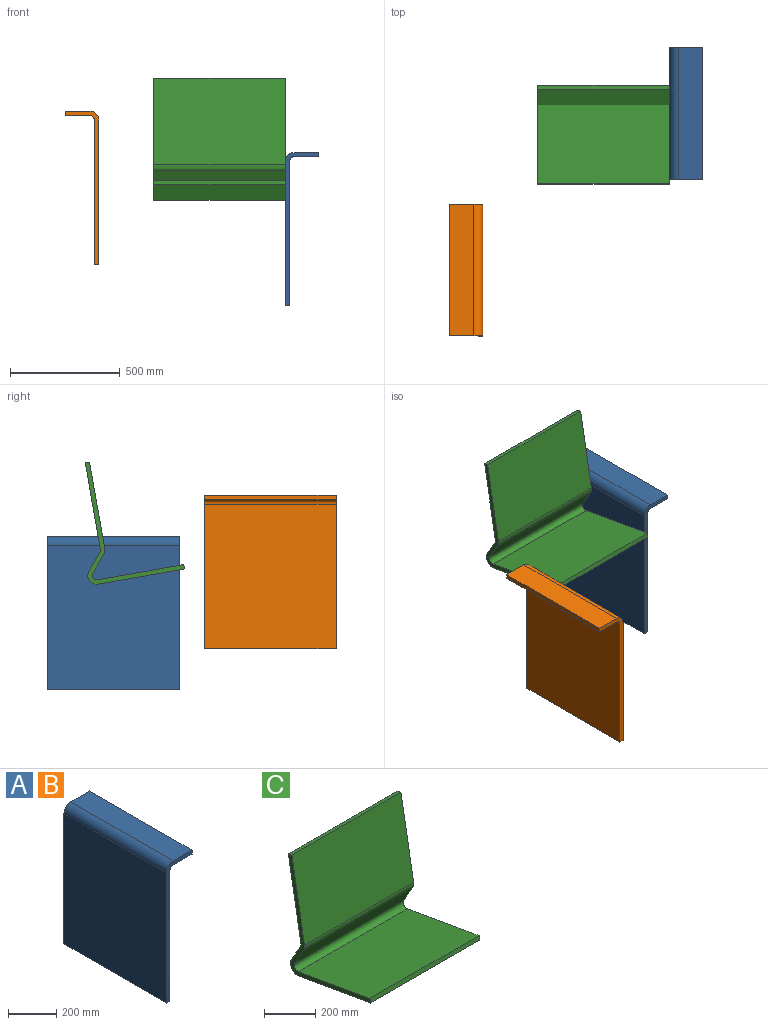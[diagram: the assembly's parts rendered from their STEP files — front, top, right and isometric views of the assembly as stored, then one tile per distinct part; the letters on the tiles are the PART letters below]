
ASSEMBLY  parts=3 mates=1
PART A: 10 faces, bbox 150x600x700 mm
  f0: plane 660x600mm, normal (-1,0,0), area 396000mm2, adj f1,f7,f8,f9
  f1: plane 600x20mm, normal (0,0,-1), area 12000mm2, adj f0,f2,f8,f9
  f2: plane 660x600mm, normal (1,0,0), area 396000mm2, adj f1,f3,f8,f9
  f3: cylinder r=20mm len=600mm, axis (0,1,0), area 18849.6mm2, adj f2,f4,f8,f9
  f4: plane 600x110mm, normal (0,0,-1), area 66000mm2, adj f3,f5,f8,f9
  f5: plane 600x20mm, normal (1,0,0), area 12000mm2, adj f4,f6,f8,f9
  f6: plane 600x110mm, normal (0,0,1), area 66000mm2, adj f5,f7,f8,f9
  f7: cylinder r=40mm len=600mm, axis (0,1,0), area 37699.1mm2, adj f0,f6,f8,f9
  f8: plane 700x150mm, normal (0,-1,0), area 16342.5mm2, adj f0,f1,f2,f3,f4,f5,f6,f7
  f9: plane 700x150mm, normal (0,1,0), area 16342.5mm2, adj f0,f1,f2,f3,f4,f5,f6,f7
PART B: same geometry as A
PART C: 14 faces, bbox 600x452.6x557.5 mm
  f0: plane 600x19.7mm, normal (0,-0.98,0.17), area 12000mm2, adj f1,f11,f12,f13
  f1: plane 600x393.92mm, normal (0,-0.17,-0.98), area 240000mm2, adj f0,f2,f12,f13
  f2: cylinder r=40mm len=600mm, axis (-1,0,0), area 54454.3mm2, adj f1,f3,f12,f13
  f3: plane 600x86.6mm, normal (0,0.87,0.5), area 60000mm2, adj f2,f4,f12,f13
  f4: cylinder r=20mm len=600mm, axis (-1,0,0), area 8377.6mm2, adj f3,f5,f12,f13
  f5: plane 600x393.92mm, normal (0,0.98,-0.17), area 240000mm2, adj f4,f6,f12,f13
  f6: plane 600x19.7mm, normal (0,0.17,0.98), area 12000mm2, adj f5,f7,f12,f13
  f7: plane 600x393.92mm, normal (0,-0.98,0.17), area 240000mm2, adj f6,f8,f12,f13
  f8: cylinder r=40mm len=600mm, axis (-1,0,0), area 16755.2mm2, adj f7,f9,f12,f13
  f9: plane 600x86.6mm, normal (0,-0.87,-0.5), area 60000mm2, adj f8,f10,f12,f13
  f10: cylinder r=20mm len=600mm, axis (-1,0,0), area 27227.1mm2, adj f9,f11,f12,f13
  f11: plane 600x393.92mm, normal (0,0.17,0.98), area 240000mm2, adj f0,f10,f12,f13
  f12: plane 557.47x452.59mm, normal (1,0,0), area 19780.2mm2, adj f0,f1,f2,f3,f4,f5,f6,f7
  f13: plane 557.47x452.59mm, normal (-1,0,0), area 19780.2mm2, adj f0,f1,f2,f3,f4,f5,f6,f7
PLACE A t=(133.3,295.22,-87.55)mm
PLACE B rot(axis=(0,0,-1),180deg) t=(-718.04,-419.79,100.42)mm
PLACE C t=(-166.7,373.19,434.15)mm
MATE fastened C.f12 <-> A.f0  axis (1,0,0) through (133.3,295.22,572.45)mm
